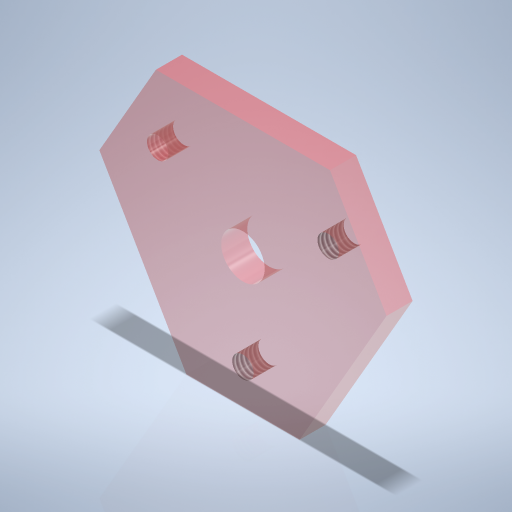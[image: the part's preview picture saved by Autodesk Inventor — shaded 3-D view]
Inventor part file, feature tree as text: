
AUTODESK INVENTOR PART (.ipt)
format: ipt  version: 2024 (Build 280153000, 153)  size: 324,608 bytes
history: native  units: mm
features: sketch x5, extrude x4, mirror x1, hole x1, projected_geometry x1
ambient origin geometry x8: Origin, YZ Plane, XZ Plane, XY Plane, X Axis, Y Axis, Z Axis, Center Point
bodies: Volumenkörper1 (feature_tree)
feature tree (12):
  sketch  "Skizze1"  dims[d0=92.0mm d1=6.0mm d2=0.0mm]
  extrude  "Extrusion1"  Depth=6.0mm TaperAngle=0.0deg
  extrude  "Extrusion6"  Depth=8.0mm
  mirror  "Spiegeln1"
  extrude  "Extrusion7"  Depth=26.0mm
  hole  "Bohrung1"  [1 undecoded]
  extrude  "Extrusion8"  Depth=10.0mm
  sketch  "Skizze2"  dims[d8=8.0mm d9=8.0mm]
  projected_geometry  "Projizierte Kontur1"
  sketch  "Skizze3"  dims[d13=4.917mm d14=12.0mm d15=4.0mm d16=2.0mm d17=90.0deg d18=8.0mm d19=0.0mm d31=26.0mm]
  sketch  "Skizze7"  dims[d36=10.0mm d37=0.0mm d38=26.0mm]
  sketch  "Skizze8"  dims[d39=10.0mm d40=0.0mm d41=8.0mm d42=8.0mm d43=8.0mm d44=15.3mm d45=30.0mm d46=10.0mm d47=10.0mm d48=0.0mm]
note: 1 required parameter value undecoded (feature->parameter linkage not recoverable at this tier; creation-order binding heuristic only, values carry confidence <= 0.55)
